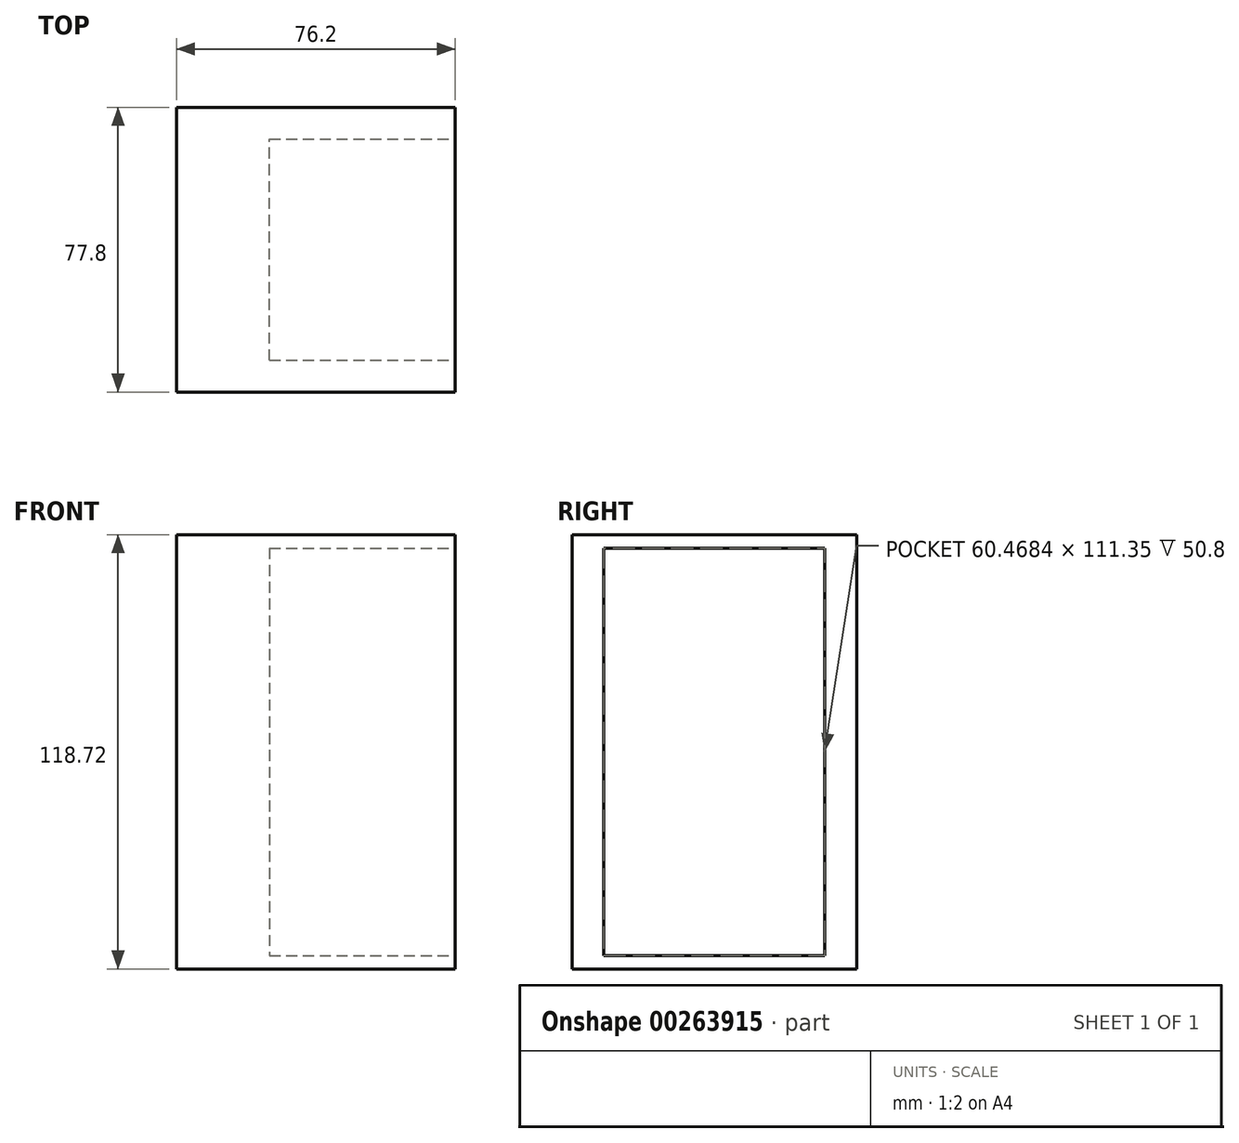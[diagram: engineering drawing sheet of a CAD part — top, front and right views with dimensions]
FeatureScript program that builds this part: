
annotation { "Feature Type Name" : "Feature", "Feature Type Description" : "" }
export const myFeature = defineFeature(function(context is Context, id is Id, definition is map)
    precondition{}
    {
        {
            var Q0;
            Q0=qCreatedBy(makeId("Right.planeOp"),FACE);
            var sketch = newSketch(context, id + "F0", { "sketchPlane" : qUnion([Q0])});
            skLineSegment(sketch, "E0.bottom", {"start": v(38.9, 59.36) * mm, "end": v(-38.9, 59.36) * mm});
            skLineSegment(sketch, "E0.top", {"start": v(38.9, -59.36) * mm, "end": v(-38.9, -59.36) * mm});
            skLineSegment(sketch, "E0.left", {"start": v(38.9, 59.36) * mm, "end": v(38.9, -59.36) * mm});
            skLineSegment(sketch, "E0.right", {"start": v(-38.9, 59.36) * mm, "end": v(-38.9, -59.36) * mm});
            skPoint(sketch, "E0.middle", {"position": v(0, 0) * mm});
            skLineSegment(sketch, "E1", {"start": v(38.9, 0) * mm, "end": v(-38.9, 0) * mm});
            skSolve(sketch);
        }
        {
            var Q0;
            Q0 = qSketchRegion(id + "F0", true);
            extrude(context, id + "F1", {"entities" : qUnion([Q0]), "oppositeDirection" : true, "depth" : 76.2 * mm});
        }
        {
            var Q0;
            Q0=qCreatedBy(makeId("Right.planeOp"),FACE);
            var sketch = newSketch(context, id + "F2", { "sketchPlane" : qUnion([Q0])});
            skLineSegment(sketch, "E2.bottom", {"start": v(-30.23, 55.68) * mm, "end": v(30.23, 55.68) * mm});
            skLineSegment(sketch, "E2.top", {"start": v(-30.23, -55.68) * mm, "end": v(30.23, -55.68) * mm});
            skLineSegment(sketch, "E2.left", {"start": v(-30.23, 55.68) * mm, "end": v(-30.23, -55.68) * mm});
            skLineSegment(sketch, "E2.right", {"start": v(30.23, 55.68) * mm, "end": v(30.23, -55.68) * mm});
            skPoint(sketch, "E2.middle", {"position": v(0, 0) * mm});
            skSolve(sketch);
        }
        {
            var Q0;
            Q0 = qSketchRegion(id + "F2", true);
            extrude(context, id + "F3", {"entities" : qUnion([Q0]), "operationType" : NewBodyOperationType.REMOVE, "oppositeDirection" : true, "depth" : 50.8 * mm});
        }
    });
